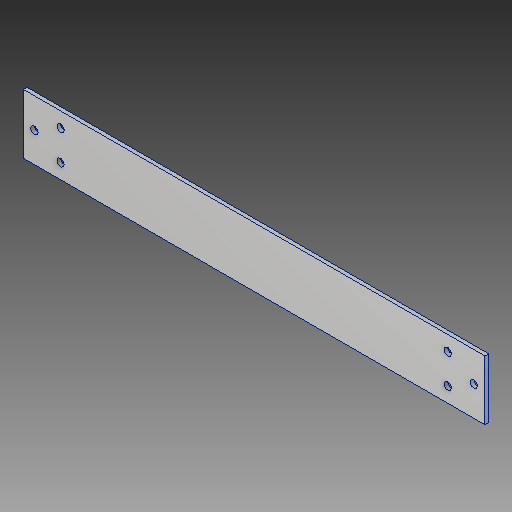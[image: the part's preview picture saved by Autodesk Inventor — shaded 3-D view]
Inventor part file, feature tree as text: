
AUTODESK INVENTOR PART (.ipt)
format: ipt  version: 2017 (Build 210142000, 142)  size: 100,352 bytes
history: native  units: in
note: dims shown in document units (in); Inventor stores cm internally (conversion verified against a paired STEP export)
features: extrude x1
ambient origin geometry x8: Origin, YZ Plane, XZ Plane, XY Plane, X Axis, Y Axis, Z Axis, Center Point
bodies: Body1 (feature_tree)
feature tree (1):
  extrude  "Extrusion2"  Depth=15.5in
